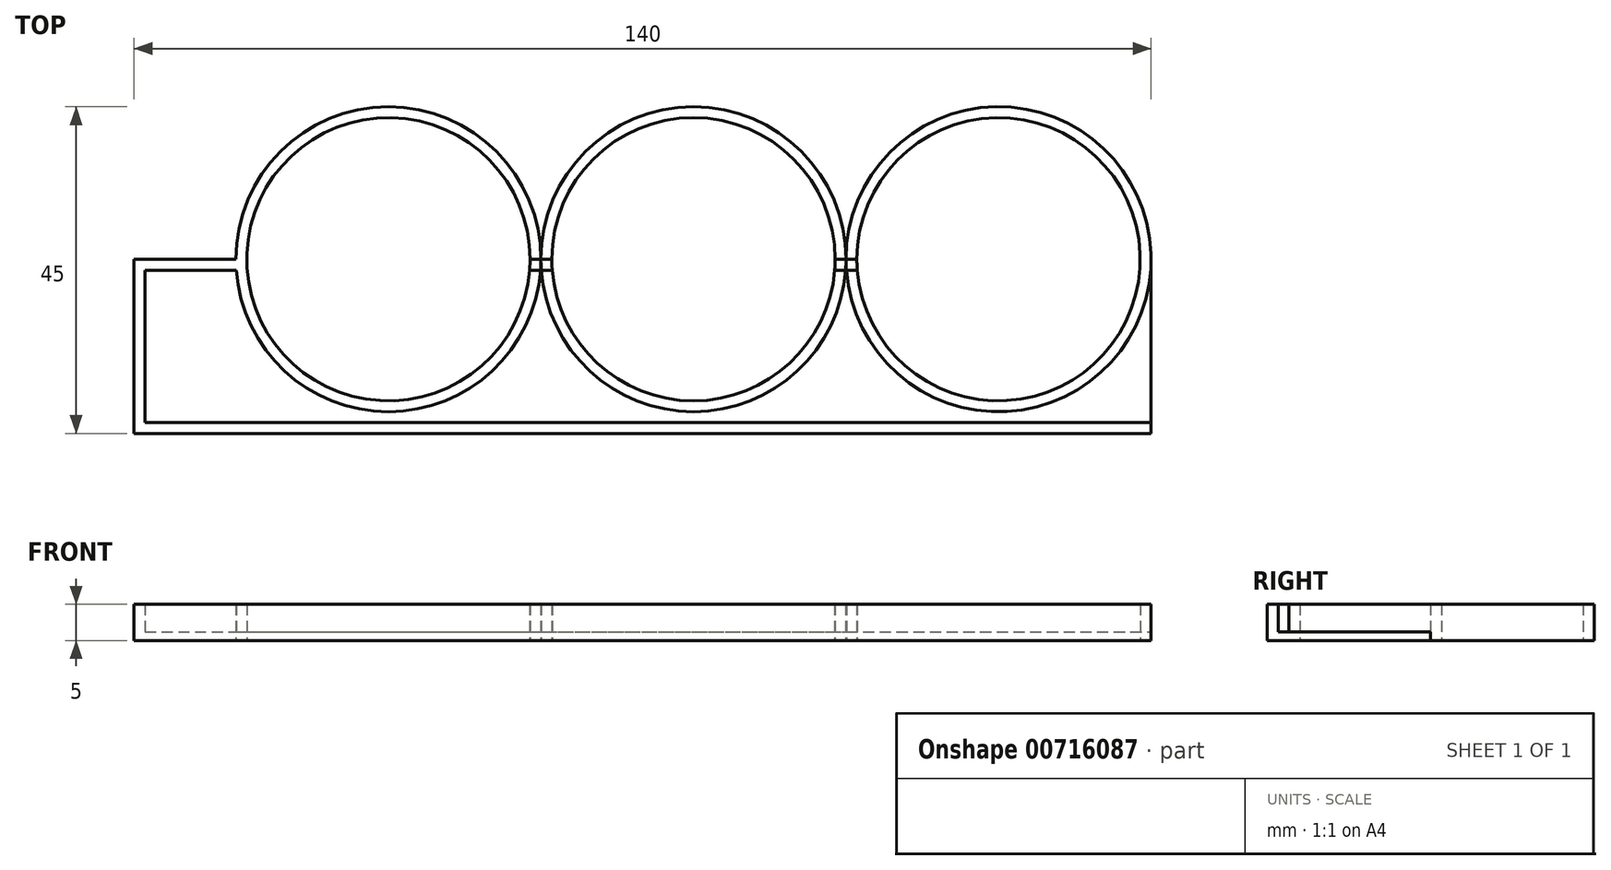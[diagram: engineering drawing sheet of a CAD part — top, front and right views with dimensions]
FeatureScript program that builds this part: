
annotation { "Feature Type Name" : "Feature", "Feature Type Description" : "" }
export const myFeature = defineFeature(function(context is Context, id is Id, definition is map)
    precondition{}
    {
        {
            var Q0;
            Q0=qCreatedBy(makeId("Top.planeOp"),FACE);
            var sketch = newSketch(context, id + "F0", { "sketchPlane" : qUnion([Q0])});
            skCircle(sketch, "E0", {"center": v(-42, 0) * mm, "radius": 19.5 * mm});
            skCircle(sketch, "E1.1.0.0", {"center": v(0, 0) * mm, "radius": 19.5 * mm});
            skCircle(sketch, "E1.2.0.0", {"center": v(42, 0) * mm, "radius": 19.5 * mm});
            skLineSegment(sketch, "E1.direction1", {"start": v(-42, 0) * mm, "end": v(0, 0) * mm, "construction": true});
            skLineSegment(sketch, "E2.bottom", {"start": v(-75.5, 21.74) * mm, "end": v(63, 21.74) * mm});
            skLineSegment(sketch, "E2.top", {"start": v(-75.5, -22.5) * mm, "end": v(64.5, -22.5) * mm});
            skLineSegment(sketch, "E2.left", {"start": v(-75.5, 21.74) * mm, "end": v(-75.5, -22.5) * mm});
            skLineSegment(sketch, "E2.right", {"start": v(63, 21.74) * mm, "end": v(63, -24) * mm});
            skLineSegment(sketch, "E3.0", {"start": v(64.5, 21.74) * mm, "end": v(64.5, -24) * mm});
            skLineSegment(sketch, "E3.1", {"start": v(-77, -24) * mm, "end": v(64.5, -24) * mm});
            skLineSegment(sketch, "E3.2", {"start": v(-77, 21.74) * mm, "end": v(-77, -24) * mm});
            skLineSegment(sketch, "E4", {"start": v(-77, 0) * mm, "end": v(64.5, 0) * mm});
            skCircle(sketch, "E5.0", {"center": v(-42, 0) * mm, "radius": 21 * mm});
            skCircle(sketch, "E6.0", {"center": v(0, 0) * mm, "radius": 21 * mm});
            skCircle(sketch, "E7.0", {"center": v(42, 0) * mm, "radius": 21 * mm});
            skLineSegment(sketch, "E8.0", {"start": v(-79, -1.5) * mm, "end": v(66.5, -1.5) * mm});
            skSolve(sketch);
        }
        {
            var Q0;
            {var subQ1=sQuery(id+"F0.wireOp",EDGE,"E2.left");var subQ5=sQuery(id+"F0.wireOp",EDGE,"E2.top");var subQ6=makeQuery(id+"F0.imprint","INTERSECT",VERTEX,{"derivedFrom":[subQ5,subQ1]});Q0=makeQuery(id+"F0.imprint","IMPRINT",FACE,{"disambiguationData":[TD([[makeQuery(id+"F0.imprint","IMPRINT",EDGE,{"disambiguationData":[TD([[subQ6,-1.0]])],"derivedFrom":subQ5}),1.0]])]});}
            extrude(context, id + "F1", {"entities" : qUnion([Q0]), "depth" : 1.2 * mm, "offsetDistance" : 25 * mm});
        }
        {
            var Q0;
            {var subQ0=sQuery(id+"F0.wireOp",EDGE,"E4");var subQ1=sQuery(id+"F0.wireOp",EDGE,"E0");var subQ2=makeQuery(id+"F0.imprint","INTERSECT",VERTEX,{"disambiguationData":[OD(0.0)],"derivedFrom":[subQ1,subQ0]});Q0=makeQuery(id+"F0.imprint","IMPRINT",FACE,{"disambiguationData":[TD([[makeQuery(id+"F0.imprint","IMPRINT",EDGE,{"disambiguationData":[TD([[subQ2,-1.0]])],"derivedFrom":subQ1}),-1.0]])]});}
            var Q1;
            {var subQ5=sQuery(id+"F0.wireOp",EDGE,"E2.top");var subQ7=sQuery(id+"F0.wireOp",EDGE,"E2.left");var subQ8=makeQuery(id+"F0.imprint","INTERSECT",VERTEX,{"derivedFrom":[subQ5,subQ7]});Q1=makeQuery(id+"F0.imprint","IMPRINT",FACE,{"disambiguationData":[TD([[makeQuery(id+"F0.imprint","IMPRINT",EDGE,{"disambiguationData":[TD([[subQ8,-1.0]])],"derivedFrom":subQ5}),-1.0]])]});}
            var Q2;
            {var subQ0=sQuery(id+"F0.wireOp",EDGE,"E4");var subQ1=sQuery(id+"F0.wireOp",EDGE,"E2.left");var subQ2=makeQuery(id+"F0.imprint","INTERSECT",VERTEX,{"derivedFrom":[subQ1,subQ0]});Q2=makeQuery(id+"F0.imprint","IMPRINT",FACE,{"disambiguationData":[TD([[makeQuery(id+"F0.imprint","IMPRINT",EDGE,{"disambiguationData":[TD([[subQ2,-1.0]])],"derivedFrom":subQ1}),1.0]])]});}
            var Q3;
            {var subQ0=sQuery(id+"F0.wireOp",EDGE,"E4");var subQ1=sQuery(id+"F0.wireOp",EDGE,"E2.left");var subQ2=makeQuery(id+"F0.imprint","INTERSECT",VERTEX,{"derivedFrom":[subQ1,subQ0]});Q3=makeQuery(id+"F0.imprint","IMPRINT",FACE,{"disambiguationData":[TD([[makeQuery(id+"F0.imprint","IMPRINT",EDGE,{"disambiguationData":[TD([[subQ2,-1.0]])],"derivedFrom":subQ1}),-1.0]])]});}
            var Q4;
            {var subQ0=sQuery(id+"F0.wireOp",EDGE,"E8.0");var subQ1=sQuery(id+"F0.wireOp",EDGE,"E0");var subQ2=makeQuery(id+"F0.imprint","INTERSECT",VERTEX,{"disambiguationData":[OD(0.0)],"derivedFrom":[subQ1,subQ0]});Q4=makeQuery(id+"F0.imprint","IMPRINT",FACE,{"disambiguationData":[TD([[makeQuery(id+"F0.imprint","IMPRINT",EDGE,{"disambiguationData":[TD([[subQ2,-1.0]])],"derivedFrom":subQ1}),-1.0]])]});}
            var Q5;
            {var subQ0=sQuery(id+"F0.wireOp",EDGE,"E5.0");var subQ1=sQuery(id+"F0.wireOp",EDGE,"E4");var subQ2=makeQuery(id+"F0.imprint","INTERSECT",VERTEX,{"disambiguationData":[OD(1.0)],"derivedFrom":[subQ1,subQ0]});Q5=makeQuery(id+"F0.imprint","IMPRINT",FACE,{"disambiguationData":[TD([[makeQuery(id+"F0.imprint","IMPRINT",EDGE,{"disambiguationData":[TD([[subQ2,-1.0]])],"derivedFrom":subQ1}),-1.0]])]});}
            var Q6;
            {var subQ0=sQuery(id+"F0.wireOp",EDGE,"E8.0");var subQ1=sQuery(id+"F0.wireOp",EDGE,"E1.1.0.0");var subQ2=makeQuery(id+"F0.imprint","INTERSECT",VERTEX,{"disambiguationData":[OD(0.0)],"derivedFrom":[subQ1,subQ0]});Q6=makeQuery(id+"F0.imprint","IMPRINT",FACE,{"disambiguationData":[TD([[makeQuery(id+"F0.imprint","IMPRINT",EDGE,{"disambiguationData":[TD([[subQ2,-1.0]])],"derivedFrom":subQ1}),-1.0]])]});}
            var Q7;
            {var subQ0=sQuery(id+"F0.wireOp",EDGE,"E8.0");var subQ1=sQuery(id+"F0.wireOp",EDGE,"E1.2.0.0");var subQ2=makeQuery(id+"F0.imprint","INTERSECT",VERTEX,{"disambiguationData":[OD(0.0)],"derivedFrom":[subQ1,subQ0]});Q7=makeQuery(id+"F0.imprint","IMPRINT",FACE,{"disambiguationData":[TD([[makeQuery(id+"F0.imprint","IMPRINT",EDGE,{"disambiguationData":[TD([[subQ2,-1.0]])],"derivedFrom":subQ1}),-1.0]])]});}
            extrude(context, id + "F2", {"entities" : qUnion([Q0, Q1, Q2, Q3, Q4, Q5, Q6, Q7]), "operationType" : NewBodyOperationType.ADD, "depth" : 5 * mm, "offsetDistance" : 25 * mm});
        }
        {
            var Q0;
            {var subQ0=sQuery(id+"F0.wireOp",EDGE,"E4");var subQ1=sQuery(id+"F0.wireOp",EDGE,"E0");var subQ2=makeQuery(id+"F0.imprint","INTERSECT",VERTEX,{"disambiguationData":[OD(0.0)],"derivedFrom":[subQ1,subQ0]});Q0=makeQuery(id+"F0.imprint","IMPRINT",FACE,{"disambiguationData":[TD([[makeQuery(id+"F0.imprint","IMPRINT",EDGE,{"disambiguationData":[TD([[subQ2,1.0]])],"derivedFrom":subQ1}),-1.0]])]});}
            var Q1;
            {var subQ0=sQuery(id+"F0.wireOp",EDGE,"E4");var subQ1=sQuery(id+"F0.wireOp",EDGE,"E1.1.0.0");var subQ2=makeQuery(id+"F0.imprint","INTERSECT",VERTEX,{"disambiguationData":[OD(0.0)],"derivedFrom":[subQ1,subQ0]});Q1=makeQuery(id+"F0.imprint","IMPRINT",FACE,{"disambiguationData":[TD([[makeQuery(id+"F0.imprint","IMPRINT",EDGE,{"disambiguationData":[TD([[subQ2,1.0]])],"derivedFrom":subQ1}),-1.0]])]});}
            var Q2;
            {var subQ0=sQuery(id+"F0.wireOp",EDGE,"E4");var subQ1=sQuery(id+"F0.wireOp",EDGE,"E1.2.0.0");var subQ2=makeQuery(id+"F0.imprint","INTERSECT",VERTEX,{"disambiguationData":[OD(0.0)],"derivedFrom":[subQ1,subQ0]});Q2=makeQuery(id+"F0.imprint","IMPRINT",FACE,{"disambiguationData":[TD([[makeQuery(id+"F0.imprint","IMPRINT",EDGE,{"disambiguationData":[TD([[subQ2,1.0]])],"derivedFrom":subQ1}),-1.0]])]});}
            var Q3;
            {var subQ0=sQuery(id+"F0.wireOp",EDGE,"E4");var subQ1=sQuery(id+"F0.wireOp",EDGE,"E1.2.0.0");var subQ2=makeQuery(id+"F0.imprint","INTERSECT",VERTEX,{"disambiguationData":[OD(1.0)],"derivedFrom":[subQ1,subQ0]});Q3=makeQuery(id+"F0.imprint","IMPRINT",FACE,{"disambiguationData":[TD([[makeQuery(id+"F0.imprint","IMPRINT",EDGE,{"disambiguationData":[TD([[subQ2,1.0]])],"derivedFrom":subQ1}),-1.0]])]});}
            extrude(context, id + "F3", {"entities" : qUnion([Q0, Q1, Q2, Q3]), "operationType" : NewBodyOperationType.ADD, "depth" : 5 * mm, "offsetDistance" : 25 * mm});
        }
        {
            var Q0;
            {var subQ0=sQuery(id+"F0.wireOp",EDGE,"E4");var subQ1=sQuery(id+"F0.wireOp",EDGE,"E0");var subQ2=makeQuery(id+"F0.imprint","INTERSECT",VERTEX,{"disambiguationData":[OD(1.0)],"derivedFrom":[subQ1,subQ0]});Q0=makeQuery(id+"F0.imprint","IMPRINT",FACE,{"disambiguationData":[TD([[makeQuery(id+"F0.imprint","IMPRINT",EDGE,{"disambiguationData":[TD([[subQ2,1.0]])],"derivedFrom":subQ1}),-1.0]])]});}
            var Q1;
            {var subQ0=sQuery(id+"F0.wireOp",EDGE,"E4");var subQ1=sQuery(id+"F0.wireOp",EDGE,"E1.1.0.0");var subQ2=makeQuery(id+"F0.imprint","INTERSECT",VERTEX,{"disambiguationData":[OD(0.0)],"derivedFrom":[subQ1,subQ0]});Q1=makeQuery(id+"F0.imprint","IMPRINT",FACE,{"disambiguationData":[TD([[makeQuery(id+"F0.imprint","IMPRINT",EDGE,{"disambiguationData":[TD([[subQ2,-1.0]])],"derivedFrom":subQ1}),-1.0]])]});}
            var Q2;
            {var subQ0=sQuery(id+"F0.wireOp",EDGE,"E4");var subQ1=sQuery(id+"F0.wireOp",EDGE,"E1.1.0.0");var subQ2=makeQuery(id+"F0.imprint","INTERSECT",VERTEX,{"disambiguationData":[OD(1.0)],"derivedFrom":[subQ1,subQ0]});Q2=makeQuery(id+"F0.imprint","IMPRINT",FACE,{"disambiguationData":[TD([[makeQuery(id+"F0.imprint","IMPRINT",EDGE,{"disambiguationData":[TD([[subQ2,1.0]])],"derivedFrom":subQ1}),-1.0]])]});}
            var Q3;
            {var subQ0=sQuery(id+"F0.wireOp",EDGE,"E4");var subQ1=sQuery(id+"F0.wireOp",EDGE,"E1.2.0.0");var subQ2=makeQuery(id+"F0.imprint","INTERSECT",VERTEX,{"disambiguationData":[OD(0.0)],"derivedFrom":[subQ1,subQ0]});Q3=makeQuery(id+"F0.imprint","IMPRINT",FACE,{"disambiguationData":[TD([[makeQuery(id+"F0.imprint","IMPRINT",EDGE,{"disambiguationData":[TD([[subQ2,-1.0]])],"derivedFrom":subQ1}),-1.0]])]});}
            extrude(context, id + "F4", {"entities" : qUnion([Q0, Q1, Q2, Q3]), "depth" : 5 * mm, "offsetDistance" : 25 * mm});
        }
    });
